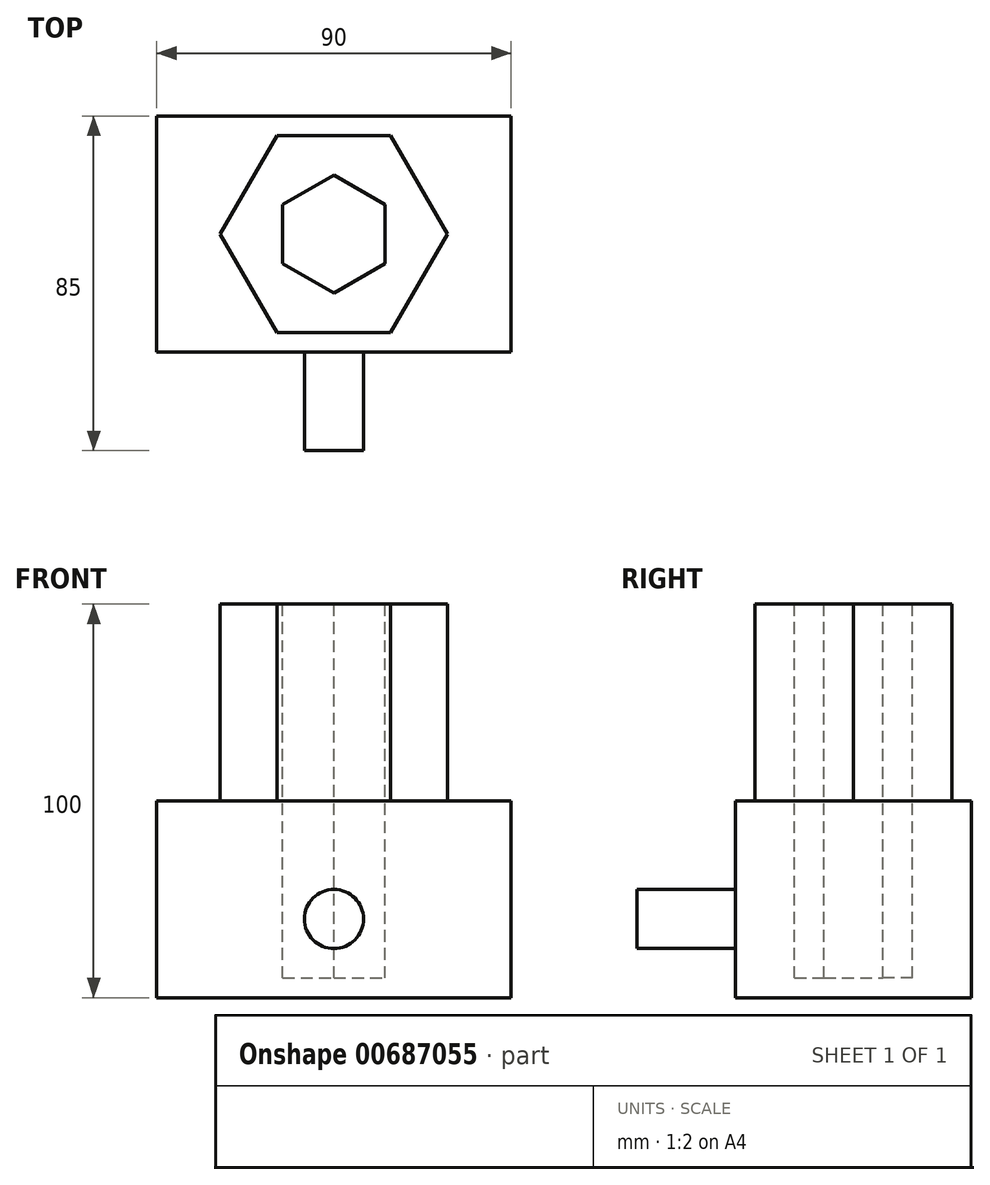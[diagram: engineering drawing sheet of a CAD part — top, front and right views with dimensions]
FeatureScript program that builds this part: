
annotation { "Feature Type Name" : "Feature", "Feature Type Description" : "" }
export const myFeature = defineFeature(function(context is Context, id is Id, definition is map)
    precondition{}
    {
        {
            var Q0;
            Q0=qCreatedBy(makeId("Top.planeOp"),FACE);
            var sketch = newSketch(context, id + "F0", { "sketchPlane" : qUnion([Q0])});
            skLineSegment(sketch, "E0.bottom", {"start": v(45, 30) * mm, "end": v(-45, 30) * mm});
            skLineSegment(sketch, "E0.top", {"start": v(45, -30) * mm, "end": v(-45, -30) * mm});
            skLineSegment(sketch, "E0.left", {"start": v(45, 30) * mm, "end": v(45, -30) * mm});
            skLineSegment(sketch, "E0.right", {"start": v(-45, 30) * mm, "end": v(-45, -30) * mm});
            skPoint(sketch, "E0.middle", {"position": v(0, 0) * mm});
            skSolve(sketch);
        }
        {
            var Q0;
            Q0 = qSketchRegion(id + "F0", true);
            extrude(context, id + "F1", {"entities" : qUnion([Q0]), "depth" : 50 * mm, "offsetDistance" : 25 * mm});
        }
        {
            var Q0;
            Q0=makeQuery(id+"F1.opExtrude","SWEPT_FACE",FACE,{"disambiguationData":[OSD([sQuery(id+"F0.wireOp",EDGE,"E0.top")])]});
            var sketch = newSketch(context, id + "F2", { "sketchPlane" : qUnion([Q0])});
            skCircle(sketch, "E1", {"center": v(0, 20) * mm, "radius": 7.5 * mm});
            skSolve(sketch);
        }
        {
            var Q0;
            Q0 = qSketchRegion(id + "F2", true);
            extrude(context, id + "F3", {"entities" : qUnion([Q0]), "operationType" : NewBodyOperationType.ADD, "depth" : 25 * mm, "offsetDistance" : 25 * mm});
        }
        {
            var Q0;
            Q0=makeQuery(id+"F1.opExtrude","CAP_FACE",FACE,{"disambiguationData":[OSD([sQuery(id+"F0.wireOp",EDGE,"E0.bottom"),sQuery(id+"F0.wireOp",EDGE,"E0.top"),sQuery(id+"F0.wireOp",EDGE,"E0.left"),sQuery(id+"F0.wireOp",EDGE,"E0.right")])],"isStart":false});
            var sketch = newSketch(context, id + "F4", { "sketchPlane" : qUnion([Q0])});
            skCircle(sketch, "E2.cCircle", {"center": v(0, 0) * mm, "radius": 25 * mm, "construction": true});
            skLineSegment(sketch, "E2.0", {"start": v(14.43, -25) * mm, "end": v(-14.43, -25) * mm});
            skLineSegment(sketch, "E2.1", {"start": v(-14.43, -25) * mm, "end": v(-28.87, 0) * mm});
            skLineSegment(sketch, "E2.2", {"start": v(-28.87, 0) * mm, "end": v(-14.43, 25) * mm});
            skLineSegment(sketch, "E2.3", {"start": v(-14.43, 25) * mm, "end": v(14.43, 25) * mm});
            skLineSegment(sketch, "E2.4", {"start": v(14.43, 25) * mm, "end": v(28.87, 0) * mm});
            skLineSegment(sketch, "E2.5", {"start": v(28.87, 0) * mm, "end": v(14.43, -25) * mm});
            skPoint(sketch, "E2.0.midPoint", {"position": v(0, -25) * mm});
            skSolve(sketch);
        }
        {
            var Q0;
            Q0 = qSketchRegion(id + "F4", true);
            extrude(context, id + "F5", {"entities" : qUnion([Q0]), "operationType" : NewBodyOperationType.ADD, "depth" : 50 * mm, "offsetDistance" : 25 * mm});
        }
        {
            var Q0;
            Q0=makeQuery(id+"F5.opExtrude","CAP_FACE",FACE,{"disambiguationData":[OSD([sQuery(id+"F4.wireOp",EDGE,"E2.0"),sQuery(id+"F4.wireOp",EDGE,"E2.1"),sQuery(id+"F4.wireOp",EDGE,"E2.2"),sQuery(id+"F4.wireOp",EDGE,"E2.3"),sQuery(id+"F4.wireOp",EDGE,"E2.4"),sQuery(id+"F4.wireOp",EDGE,"E2.5")])],"isStart":false});
            var sketch = newSketch(context, id + "F6", { "sketchPlane" : qUnion([Q0])});
            skCircle(sketch, "E3.cCircle", {"center": v(0, 0) * mm, "radius": 13 * mm, "construction": true});
            skLineSegment(sketch, "E3.0", {"start": v(0, 15) * mm, "end": v(13, 7.5) * mm});
            skLineSegment(sketch, "E3.1", {"start": v(13, 7.5) * mm, "end": v(13, -7.5) * mm});
            skLineSegment(sketch, "E3.2", {"start": v(13, -7.5) * mm, "end": v(0, -15) * mm});
            skLineSegment(sketch, "E3.3", {"start": v(0, -15) * mm, "end": v(-13, -7.5) * mm});
            skLineSegment(sketch, "E3.4", {"start": v(-13, -7.5) * mm, "end": v(-13, 7.5) * mm});
            skLineSegment(sketch, "E3.5", {"start": v(-13, 7.5) * mm, "end": v(0, 15) * mm});
            skPoint(sketch, "E3.0.midPoint", {"position": v(6.5, 11.25) * mm});
            skSolve(sketch);
        }
        {
            var Q0;
            Q0 = qSketchRegion(id + "F6", true);
            extrude(context, id + "F7", {"entities" : qUnion([Q0]), "operationType" : NewBodyOperationType.REMOVE, "oppositeDirection" : true, "depth" : 95 * mm, "offsetDistance" : 25 * mm});
        }
    });
